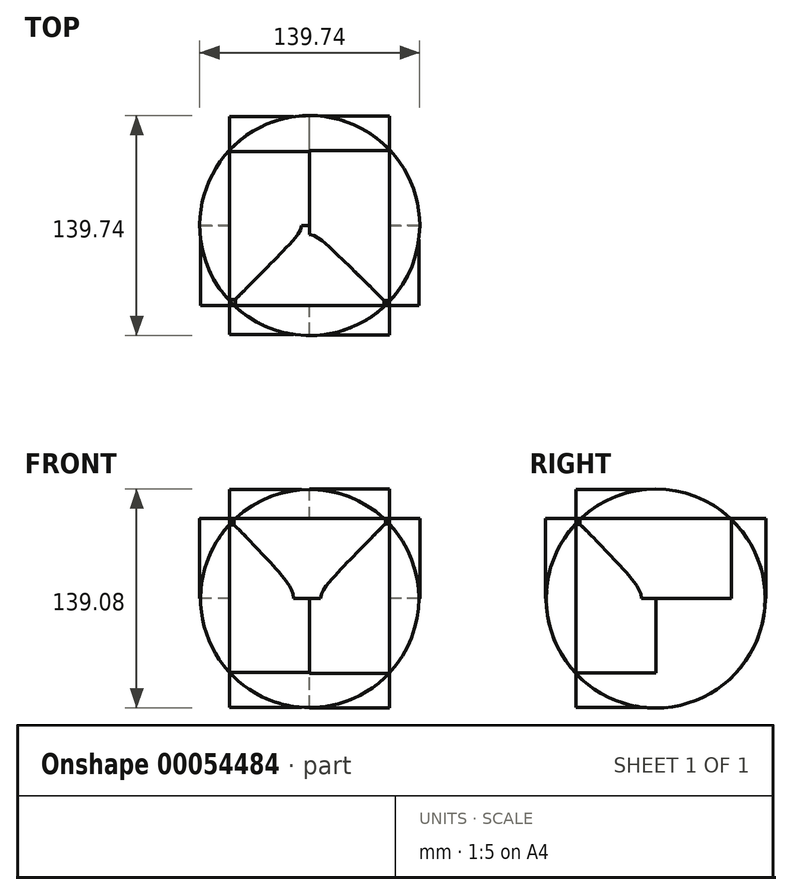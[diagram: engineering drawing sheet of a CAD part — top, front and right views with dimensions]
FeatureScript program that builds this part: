
annotation { "Feature Type Name" : "Feature", "Feature Type Description" : "" }
export const myFeature = defineFeature(function(context is Context, id is Id, definition is map)
    precondition{}
    {
        {
            var Q0;
            Q0=qCreatedBy(makeId("Front.planeOp"),FACE);
            var sketch = newSketch(context, id + "F0", { "sketchPlane" : qUnion([Q0])});
            skCircle(sketch, "E0", {"center": v(0, 0) * mm, "radius": 69.3 * mm});
            skSolve(sketch);
        }
        {
            var Q0;
            Q0=makeQuery(id+"F0.imprint","IMPRINT",FACE,{"disambiguationData":[TD([[makeQuery(id+"F0.imprint","IMPRINT",EDGE,{"derivedFrom":sQuery(id+"F0.wireOp",EDGE,"E0")}),1.0]])]});
            extrude(context, id + "F1", {"entities" : qUnion([Q0]), "depth" : 50.8 * mm});
        }
        {
            var Q0;
            Q0=qCreatedBy(makeId("Top.planeOp"),FACE);
            var sketch = newSketch(context, id + "F2", { "sketchPlane" : qUnion([Q0])});
            skCircle(sketch, "E1", {"center": v(0, 0) * mm, "radius": 69.38 * mm});
            skSolve(sketch);
        }
        {
            var Q0;
            Q0=makeQuery(id+"F2.imprint","IMPRINT",FACE,{"disambiguationData":[TD([[makeQuery(id+"F2.imprint","IMPRINT",EDGE,{"derivedFrom":sQuery(id+"F2.wireOp",EDGE,"E1")}),1.0]])]});
            extrude(context, id + "F3", {"entities" : qUnion([Q0]), "operationType" : NewBodyOperationType.ADD, "depth" : 50.8 * mm});
        }
        {
            var Q0;
            Q0=qCreatedBy(makeId("Right.planeOp"),FACE);
            var sketch = newSketch(context, id + "F4", { "sketchPlane" : qUnion([Q0])});
            skCircle(sketch, "E2", {"center": v(0, 0) * mm, "radius": 69.54 * mm});
            skSolve(sketch);
        }
        {
            var Q0;
            Q0 = qSketchRegion(id + "F4", true);
            extrude(context, id + "F5", {"entities" : qUnion([Q0]), "operationType" : NewBodyOperationType.ADD, "depth" : 50.8 * mm});
        }
        {
            var Q0;
            Q0=qCreatedBy(makeId("Right.planeOp"),FACE);
            var sketch = newSketch(context, id + "F6", { "sketchPlane" : qUnion([Q0])});
            skCircle(sketch, "E3", {"center": v(0, 0) * mm, "radius": 69.11 * mm});
            skSolve(sketch);
        }
        {
            var Q0;
            Q0=makeQuery(id+"F6.imprint","IMPRINT",FACE,{"disambiguationData":[TD([[makeQuery(id+"F6.imprint","IMPRINT",EDGE,{"derivedFrom":sQuery(id+"F6.wireOp",EDGE,"E3")}),1.0]])]});
            extrude(context, id + "F7", {"entities" : qUnion([Q0]), "operationType" : NewBodyOperationType.ADD, "oppositeDirection" : true, "depth" : 50.8 * mm});
        }
        {
            var Q0;
            Q0=qCreatedBy(makeId("Top.planeOp"),FACE);
            var sketch = newSketch(context, id + "F8", { "sketchPlane" : qUnion([Q0])});
            skCircle(sketch, "E4", {"center": v(0, 0) * mm, "radius": 69.87 * mm});
            skSolve(sketch);
        }
        {
            var Q0;
            Q0=makeQuery(id+"F8.imprint","IMPRINT",FACE,{"disambiguationData":[TD([[makeQuery(id+"F8.imprint","IMPRINT",EDGE,{"derivedFrom":sQuery(id+"F8.wireOp",EDGE,"E4")}),1.0]])]});
            extrude(context, id + "F9", {"entities" : qUnion([Q0]), "operationType" : NewBodyOperationType.ADD, "depth" : 50.8 * mm});
        }
        {
            var Q0;
            Q0=qCreatedBy(makeId("Front.planeOp"),FACE);
            var sketch = newSketch(context, id + "F10", { "sketchPlane" : qUnion([Q0])});
            skCircle(sketch, "E5", {"center": v(0, 0) * mm, "radius": 69.06 * mm});
            skSolve(sketch);
        }
        {
            var Q0;
            Q0=makeQuery(id+"F10.imprint","IMPRINT",FACE,{"disambiguationData":[TD([[makeQuery(id+"F10.imprint","IMPRINT",EDGE,{"derivedFrom":sQuery(id+"F10.wireOp",EDGE,"E5")}),1.0]])]});
            extrude(context, id + "F11", {"entities" : qUnion([Q0]), "operationType" : NewBodyOperationType.ADD, "depth" : 50.8 * mm});
        }
    });
